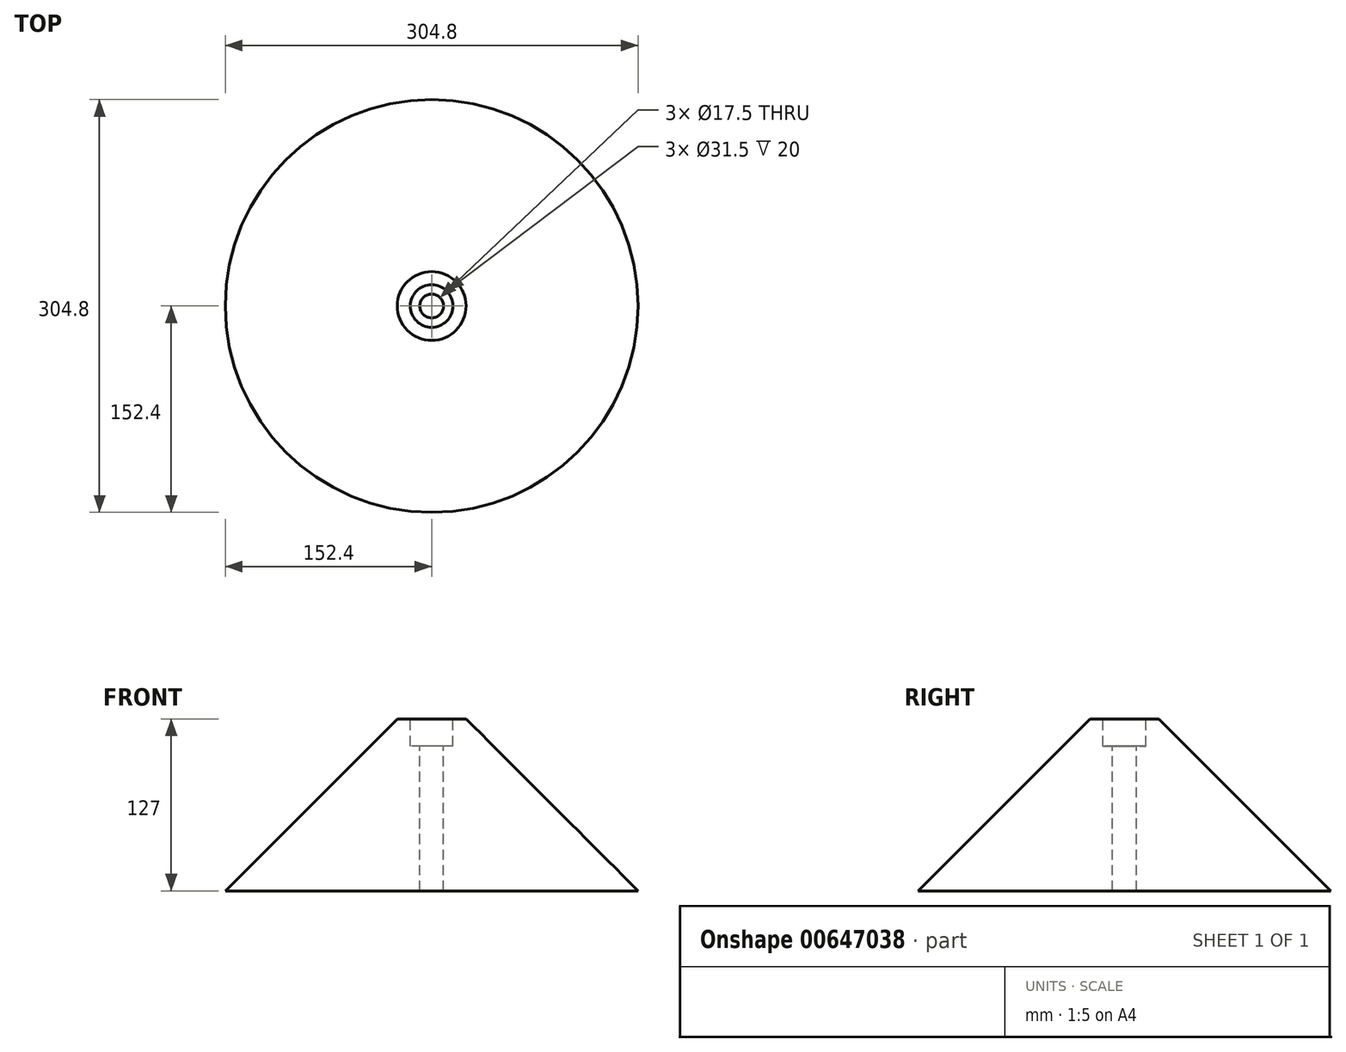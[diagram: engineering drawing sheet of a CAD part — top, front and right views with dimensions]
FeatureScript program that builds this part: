
annotation { "Feature Type Name" : "Feature", "Feature Type Description" : "" }
export const myFeature = defineFeature(function(context is Context, id is Id, definition is map)
    precondition{}
    {
        {
            var Q0;
            Q0=qCreatedBy(makeId("Top.planeOp"),FACE);
            var sketch = newSketch(context, id + "F0", { "sketchPlane" : qUnion([Q0])});
            skCircle(sketch, "E0", {"center": v(0, 0) * mm, "radius": 152.4 * mm});
            skSolve(sketch);
        }
        {
            var Q0;
            Q0=makeQuery(id+"F0.imprint","IMPRINT",FACE,{"disambiguationData":[TD([[makeQuery(id+"F0.imprint","IMPRINT",EDGE,{"derivedFrom":sQuery(id+"F0.wireOp",EDGE,"E0")}),1.0]])]});
            extrude(context, id + "F1", {"entities" : qUnion([Q0]), "depth" : 127 * mm, "offsetDistance" : 25.4 * mm});
        }
        {
            var Q0;
            Q0=makeQuery(id+"F1.opExtrude","CAP_FACE",FACE,{"disambiguationData":[OSD([sQuery(id+"F0.wireOp",EDGE,"E0")])],"isStart":false});
            var sketch = newSketch(context, id + "F2", { "sketchPlane" : qUnion([Q0])});
            skPoint(sketch, "E1", {"position": v(0, 0) * mm});
            skSolve(sketch);
        }
        {
            var Q0;
            Q0=sQuery(id+"F2.wireOp",VERTEX,"E1");
            var Q1;
            Q1=makeQuery(id+"F1.opExtrude","SWEPT_BODY",BODY,{"disambiguationData":[OSD([sQuery(id+"F0.wireOp",EDGE,"E0")])]});
            hole(context, id + "F3", {"style" : HoleStyle.C_BORE, "endStyle" : HoleEndStyle.THROUGH, "standardTappedOrClearance" : lookupTablePath({ "standard" : "ISO", "engagement" : "75%", "pitch" : "2.5 mm", "size" : "M20", "type" : "Tapped" }), "standardBlindInLast" : lookupTablePath({ "standard" : "ISO", "engagement" : "75%", "pitch" : "2.5 mm", "size" : "M20", "type" : "Tapped" }), "holeDiameter" : 17.5 * mm, "cBoreDiameter" : 31.5 * mm, "cBoreDepth" : 20 * mm, "majorDiameter" : 20 * mm, "showTappedDepth" : true, "isTappedThrough" : true, "tappedDepth" : 12.7 * mm, "tapClearance" : 3, "startFromSketch" : true, "locations" : qUnion([Q0]), "scope" : qUnion([Q1])});
        }
        {
            var Q0;
            Q0=makeQuery(id+"F1.opExtrude","CAP_EDGE",EDGE,{"disambiguationData":[OSD([sQuery(id+"F0.wireOp",EDGE,"E0")])],"isStart":false});
            chamfer(context, id + "F4", {"entities" : qUnion([Q0]), "width" : 127 * mm, "tangentPropagation" : true});
        }
    });
